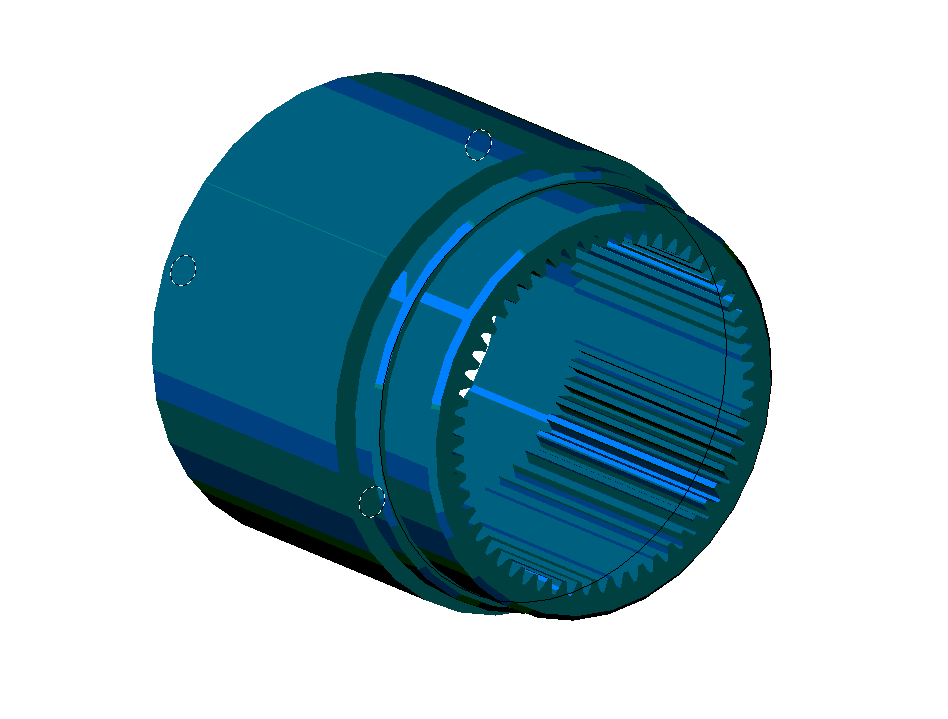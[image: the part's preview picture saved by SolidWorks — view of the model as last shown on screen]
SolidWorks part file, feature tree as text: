
SOLIDWORKS PART (.sldprt)
format: sldprt  version: not decoded by parser v0  size: 388,608 bytes
history: native  units: mm
features: sketch x12, cut_extrude x5, plane x4, extrude x3, chamfer x3, thread x2, hole x2, material x1, pattern_circular x1 (+10 scaffold rows collapsed)
feature tree (43):
  scaffold x10  (default folders/planes/origin — collapsed)
  material  "Matériau <non spécifié>"
  plane  "Plan1"
  plane  "Plan2"
  plane  "Plan3"
  sketch  "Esquisse1"  dims[D1=38.0mm]
  extrude  "Base-Extrusion"  Depth=33.9mm
  sketch  "Esquisse2"  dims[D1=28.0mm]
  cut_extrude  "Enlèv. mat.-Extru.1"  [1 undecoded]
  sketch  "Esquisse3"  dims[D1=30.0mm]
  cut_extrude  "Enlèv. mat.-Extru.2"  Depth=11.9mm
  sketch  "Esquisse4"  dims[D1=34.0mm]
  cut_extrude  "Enlèv. mat.-Extru.3"  Depth=24mm
  plane  "Plan4"  Offset=0.8mm
  sketch  "Esquisse5"  dims[D1=36.0mm]
  extrude  "Boss.-Extru.1"  [1 undecoded]
  thread  "Représentation de filetage2"  [2 undecoded]
  chamfer  "Chanfrein2"  Distance=0.5mm Angle=45deg
  hole  "Perçage1"  Diameter=2.05mm Depth=10.25mm
  sketch  "Esquisse7"  dims[D1=17.0mm]
  sketch  "Esquisse6"  dims[hole-wizard template sketch: 46 standard entries collapsed; hole parameters kept: c15.Diamètre du perçage=2.05mm c15.Profondeur du perçage=10.25mm c15.D3=~14.816244mm c15.Angle de pointe=118.0deg]
  thread  "Représentation de filetage1"  Diameter=8mm  [1 undecoded]
  pattern_circular  "Répétition circulaire1"  Count=3 Angle=120deg
  chamfer  "Chanfrein1"  Distance=0.5mm Angle=45deg
  chamfer  "Chanfrein4"  Distance=0.5mm Angle=45deg
  sketch  "Esquisse8"
  sketch  "Esquisse9"  dims[Z=57.0mm m=0.5mm Alpha=20.0mm Alpha_rad=~0.349066mm PI=~3.141593mm R=14.25mm RT=14.875mm RP=13.75mm Rb=~13.39062mm E=~0.785398mm Eb=~1.137191mm As=~0.450545mm Et=~0.276071mm Ap=~3.157895mm Ab=~1.449978mm At=~5.252413mm k=15.0mm]
  sketch  "Esquisse10"  dims[D1=29.75mm]
  cut_extrude  "Enlèv. mat.-Extru.4"  Depth=22mm
  sketch  "Esquisse11"  dims[c1.D7=~26.109396mm c1.D1=13.75mm c1.D4=~19.714326mm c2.D1=~29.376396mm c3.D1=~5.114687deg c3.D2=~29.376396mm c4.D2=~11.734276deg c4.D3=~29.376396mm c5.D3=~14.703049deg c5.D4=~17.959793mm c6.D4=~16.363636deg c6.D5=~13.39062mm c6.D6=14.25mm c6.D7=~26.109403mm c6.D1=~26.109403mm c7.D1=~174.885313deg c8.D1=~26.109403mm c9.D1=~5.114687deg c10.D1=24.0mm c10.D2=~17.959793mm c11.D2=~0.724989deg c11.D3=~22.451883mm c12.D3=~1.578947deg c12.D7=~26.109403mm c13.D7=~5.114687deg c14.D7=~29.376396mm c15.D7=~5.114687deg c16.D7=~29.376396mm c17.D7=~5.114687deg c18.D7=~29.376396mm c19.D7=~5.114687deg c20.D7=~29.376396mm c21.D7=~5.114687deg c22.D7=~29.376396mm c23.D7=~2.626207deg c23.D8=19.5mm c23.D1=24.0mm]
  extrude  "Boss.-Extru.2"  Depth=22mm
  hole  "Répétition circulaire2"  Diameter=57
  sketch  "Esquisse12"  dims[D1=28.5mm]
  cut_extrude  "Enlèv. mat.-Extru.5"  Depth=22mm
decode coverage: 24 of 28 modeling features carry decoded parameters
note: ~ marks probable driven/reference dimensions
note: 5 parameter values undecoded
summary: no parameter record found for 3 features
note: suppression state not decoded; provenance and decode notes live in map.json
